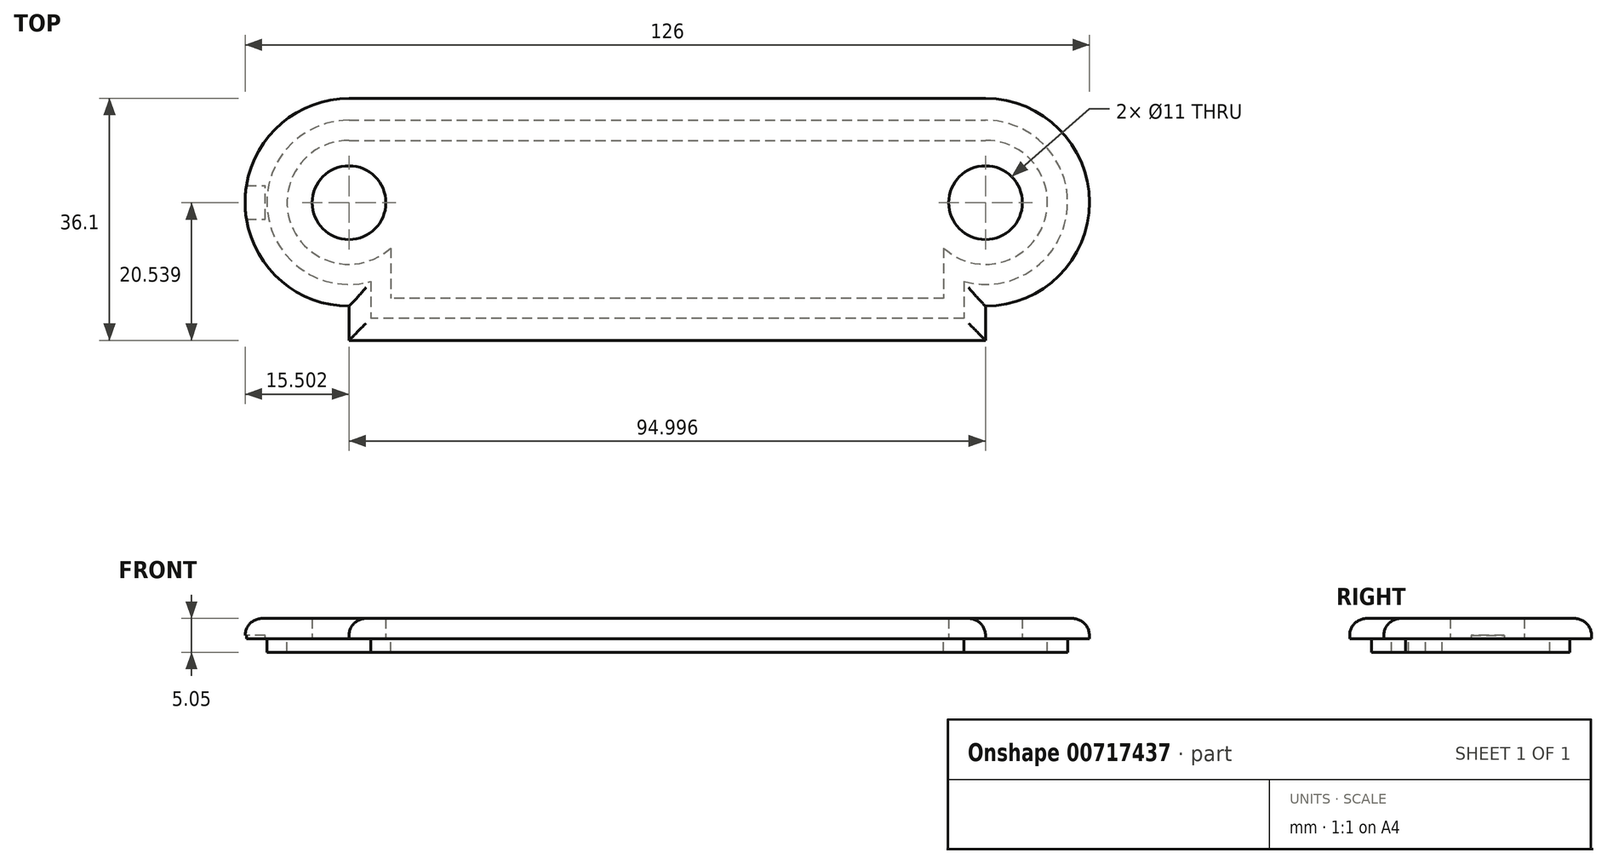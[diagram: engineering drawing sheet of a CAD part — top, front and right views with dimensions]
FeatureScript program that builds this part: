
annotation { "Feature Type Name" : "Feature", "Feature Type Description" : "" }
export const myFeature = defineFeature(function(context is Context, id is Id, definition is map)
    precondition{}
    {
        {
            var Q0;
            Q0=qCreatedBy(makeId("Top.planeOp"),FACE);
            var sketch = newSketch(context, id + "F0", { "sketchPlane" : qUnion([Q0])});
            skLineSegment(sketch, "E0.bottom", {"start": v(47.5, 18.05) * mm, "end": v(-47.5, 18.05) * mm});
            skLineSegment(sketch, "E0.top", {"start": v(47.5, -18.05) * mm, "end": v(-47.5, -18.05) * mm});
            skLineSegment(sketch, "E0.left", {"start": v(47.5, 18.05) * mm, "end": v(47.5, -18.05) * mm});
            skLineSegment(sketch, "E0.right", {"start": v(-47.5, 18.05) * mm, "end": v(-47.5, -18.05) * mm});
            skPoint(sketch, "E0.middle", {"position": v(0, 0) * mm});
            skCircle(sketch, "E1", {"center": v(-47.5, 2.55) * mm, "radius": 15.5 * mm});
            skCircle(sketch, "E2", {"center": v(47.5, 2.55) * mm, "radius": 15.5 * mm});
            skSolve(sketch);
        }
        {
            var Q0;
            Q0=qSketchRegion(id+"F0",true);
            extrude(context, id + "F1", {"entities" : qUnion([Q0]), "depth" : 3.05 * mm, "offsetDistance" : 25.4 * mm});
        }
        {
            var Q0;
            Q0=makeQuery(id+"F1.opExtrude","CAP_EDGE",EDGE,{"disambiguationData":[OSD([sQuery(id+"F0.wireOp",EDGE,"E1")])],"isStart":false});
            var Q1;
            Q1=makeQuery(id+"F1.opExtrude","CAP_EDGE",EDGE,{"disambiguationData":[OSD([sQuery(id+"F0.wireOp",EDGE,"E2")])],"isStart":false});
            var Q2;
            Q2=makeQuery(id+"F1.opExtrude","CAP_FACE",FACE,{"disambiguationData":[OSD([sQuery(id+"F0.wireOp",EDGE,"E0.bottom"),sQuery(id+"F0.wireOp",EDGE,"E0.top"),sQuery(id+"F0.wireOp",EDGE,"E0.left"),sQuery(id+"F0.wireOp",EDGE,"E0.right"),sQuery(id+"F0.wireOp",EDGE,"E1"),sQuery(id+"F0.wireOp",EDGE,"E2")])],"isStart":false});
            fillet(context, id + "F2", {"entities" : qUnion([Q0, Q1, Q2]), "radius" : 2.54 * mm, "tangentPropagation" : true, "allowEdgeOverflow" : false});
        }
        {
            var Q0;
            Q0=qCreatedBy(makeId("Top.planeOp"),FACE);
            var sketch = newSketch(context, id + "F3", { "sketchPlane" : qUnion([Q0])});
            skCircle(sketch, "E3", {"center": v(-47.5, 2.49) * mm, "radius": 5.5 * mm});
            skCircle(sketch, "E4", {"center": v(47.5, 2.49) * mm, "radius": 5.5 * mm});
            skSolve(sketch);
        }
        {
            var Q0;
            Q0 = qSketchRegion(id + "F3", true);
            extrude(context, id + "F4", {"entities" : qUnion([Q0]), "operationType" : NewBodyOperationType.REMOVE, "depth" : 3.05 * mm, "offsetDistance" : 25.4 * mm});
        }
        {
            var Q0;
            Q0=qCreatedBy(makeId("Top.planeOp"),FACE);
            var sketch = newSketch(context, id + "F5", { "sketchPlane" : qUnion([Q0])});
            skLineSegment(sketch, "E5.left", {"start": v(47.5, 2.55) * mm, "end": v(47.5, 2.52) * mm});
            skPoint(sketch, "E5.middle", {"position": v(0, 0) * mm});
            skPoint(sketch, "E6.end.orphan", {"position": v(-47.5, 2.55) * mm});
            skLineSegment(sketch, "E7", {"start": v(47.5, 18.05) * mm, "end": v(47.5, 18.05) * mm});
            skLineSegment(sketch, "E8", {"start": v(47.5, 2.52) * mm, "end": v(47.5, 2.52) * mm});
            skArc(sketch, "E9.0", {"start": v(-47.5, 14.8) * mm, "mid": v(-59.64, 0.9) * mm, "end": v(-44.25, -9.26) * mm});
            skArc(sketch, "E9.1", {"start": v(44.25, -9.26) * mm, "mid": v(59.64, 0.9) * mm, "end": v(47.5, 14.8) * mm});
            skLineSegment(sketch, "E9.2", {"start": v(44.25, -9.26) * mm, "end": v(44.25, -14.8) * mm});
            skLineSegment(sketch, "E9.3", {"start": v(44.25, -14.8) * mm, "end": v(-44.25, -14.8) * mm});
            skLineSegment(sketch, "E9.4", {"start": v(-44.25, -9.26) * mm, "end": v(-44.25, -14.8) * mm});
            skLineSegment(sketch, "E10", {"start": v(-47.5, 14.8) * mm, "end": v(47.5, 14.8) * mm});
            skLineSegment(sketch, "E11.0", {"start": v(41.25, -4.27) * mm, "end": v(41.25, -11.8) * mm});
            skLineSegment(sketch, "E11.1", {"start": v(-41.25, -4.27) * mm, "end": v(-41.25, -11.8) * mm});
            skArc(sketch, "E11.2", {"start": v(-47.5, 11.8) * mm, "mid": v(-56.12, -0.8) * mm, "end": v(-41.25, -4.27) * mm});
            skLineSegment(sketch, "E11.3", {"start": v(41.25, -11.8) * mm, "end": v(-41.25, -11.8) * mm});
            skLineSegment(sketch, "E11.4", {"start": v(-47.5, 11.8) * mm, "end": v(47.5, 11.8) * mm});
            skArc(sketch, "E11.5", {"start": v(41.25, -4.27) * mm, "mid": v(56.12, -0.8) * mm, "end": v(47.5, 11.8) * mm});
            skSolve(sketch);
        }
        {
            var Q0;
            Q0=makeQuery(id+"F5.imprint","IMPRINT",FACE,{"disambiguationData":[TD([[makeQuery(id+"F5.imprint","IMPRINT",EDGE,{"derivedFrom":sQuery(id+"F5.wireOp",EDGE,"E9.0")}),1.0]])]});
            extrude(context, id + "F6", {"entities" : qUnion([Q0]), "operationType" : NewBodyOperationType.ADD, "oppositeDirection" : true, "depth" : 2 * mm, "offsetDistance" : 25.4 * mm});
        }
        {
            var Q0;
            Q0=qCreatedBy(makeId("Right.planeOp"),FACE);
            cPlane(context, id + "F7", {"entities" : qUnion([Q0]), "cplaneType" : CPlaneType.OFFSET, "offset" : 63 * mm, "oppositeDirection" : true, "width" : 152.4 * mm, "height" : 152.4 * mm});
        }
        {
            var Q0;
            Q0=qCreatedBy(id+"F7.planeOp",FACE);
            var sketch = newSketch(context, id + "F8", { "sketchPlane" : qUnion([Q0])});
            skLineSegment(sketch, "E12.bottom", {"start": v(0.05, -0.5) * mm, "end": v(5.05, -0.5) * mm});
            skLineSegment(sketch, "E12.top", {"start": v(0.05, 0.5) * mm, "end": v(5.05, 0.5) * mm});
            skLineSegment(sketch, "E12.left", {"start": v(0.05, -0.5) * mm, "end": v(0.05, 0.5) * mm});
            skLineSegment(sketch, "E12.right", {"start": v(5.05, -0.5) * mm, "end": v(5.05, 0.5) * mm});
            skPoint(sketch, "E12.middle", {"position": v(2.55, 0) * mm});
            skSolve(sketch);
        }
        {
            var Q0;
            Q0 = qSketchRegion(id + "F8", true);
            extrude(context, id + "F9", {"entities" : qUnion([Q0]), "operationType" : NewBodyOperationType.REMOVE, "depth" : 3 * mm, "offsetDistance" : 25.4 * mm});
        }
    });
